# Revit family: 63_UN_Pendant_BLOSSUM PS_B_M_Signify
name_source: partatom
category: Lighting Fixtures
units: mm (PartAtom-declared; Revit-internal decimal feet)

## family parameters
Always vertical = Yes
Cut with Voids When Loaded = Yes
Light Source = No
OmniClass Number = 23.80.70.11.14.11
OmniClass Title = Downlights
Part Type = Normal
Room Calculation Point = Yes
Round Connector Dimension = Use Diameter
Shared = No
Work Plane-Based = No

## types (1)
- BLOSSUM PS_B_M
    Apparent Load = 19 VA
    Assembly Code = 63.0
    Description = Bulb is not included, reference bulb used: MASVLELEDBulb D5.9-60W E27 927A60FR G UK
    Hood_Housing_Material = 55% recycled or bio-circular policarbonate
    IfcExportAs = IfcLightFixtureType
    IfcExportType = USERDEFINED
    Lamp = LED
    Light Source = 3DPrinted Blossom M - Geometry : -
    Manufacturer = Signify
    Model = 3DPrinted
    Pendant_Material = 55% recycled or bio-circular policarbonate
    Type Comments = Available in the below Philips MyCreation colors: BK402 – Satin Black, GR402 – Satin Grey, WH401 - Satin White, GR000 - Smokey Grey, BZ410 - Satin Bronze, BS410 - Satin Brass, PK400 - Satin Rose, GN402 - Satin sage
    URL = https://pro.mycreation.lighting.philips.com
    Voltage = 230 V
    Wattage Comments = 19 W

## geometry (parser evidence)
native form markers: Sweep x13
no freeform markers — native parametric forms only
